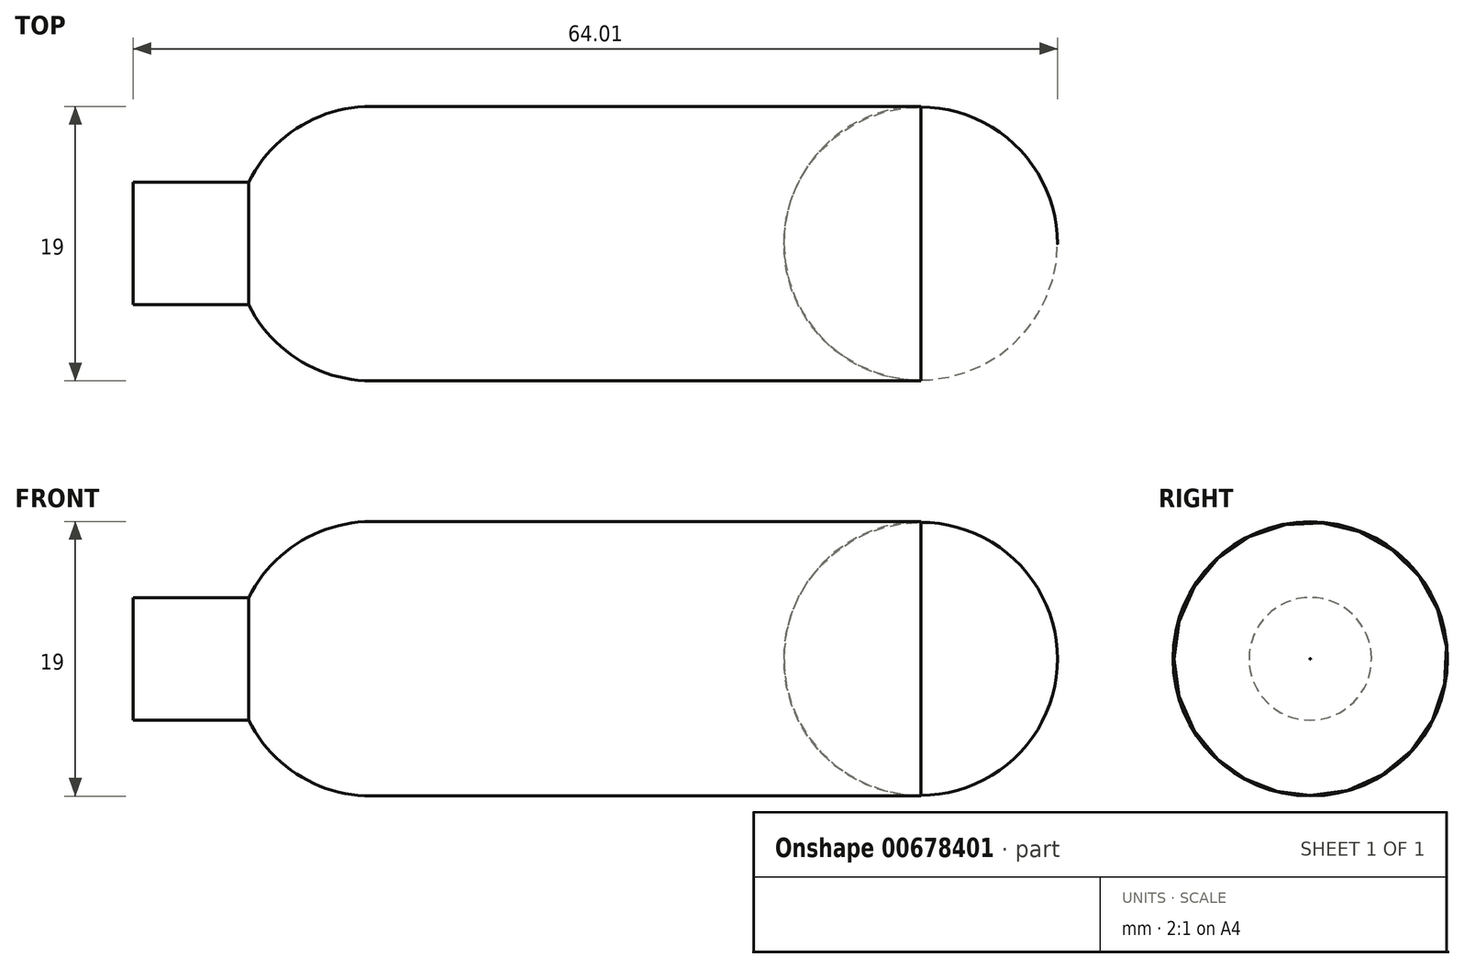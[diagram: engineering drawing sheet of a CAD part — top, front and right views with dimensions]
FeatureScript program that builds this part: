
annotation { "Feature Type Name" : "Feature", "Feature Type Description" : "" }
export const myFeature = defineFeature(function(context is Context, id is Id, definition is map)
    precondition{}
    {
        {
            var Q0;
            Q0=qCreatedBy(makeId("Front.planeOp"),FACE);
            var sketch = newSketch(context, id + "F0", { "sketchPlane" : qUnion([Q0])});
            skLineSegment(sketch, "E0", {"start": v(0, 0) * mm, "end": v(64, 0) * mm});
            skLineSegment(sketch, "E1", {"start": v(0, 0) * mm, "end": v(0, 4.24) * mm});
            skLineSegment(sketch, "E2", {"start": v(0, 4.24) * mm, "end": v(8, 4.24) * mm});
            skLineSegment(sketch, "E3", {"start": v(64, 0) * mm, "end": v(64, 9.5) * mm});
            skLineSegment(sketch, "E4", {"start": v(64, 9.5) * mm, "end": v(8, 9.5) * mm});
            skLineSegment(sketch, "E5", {"start": v(8, 9.5) * mm, "end": v(8, 4.24) * mm});
            skPoint(sketch, "E6", {"position": v(36, 9.5) * mm});
            skLineSegment(sketch, "E7", {"start": v(36, 9.5) * mm, "end": v(56, 9.5) * mm});
            skLineSegment(sketch, "E8", {"start": v(36, 9.5) * mm, "end": v(16, 9.5) * mm});
            skSolve(sketch);
        }
        {
            var Q0;
            Q0=makeQuery(id+"F0.imprint","IMPRINT",FACE,{"disambiguationData":[TD([[makeQuery(id+"F0.imprint","IMPRINT",EDGE,{"derivedFrom":sQuery(id+"F0.wireOp",EDGE,"E0")}),1.0]])]});
            var Q1;
            Q1=sQuery(id+"F0.wireOp",EDGE,"E0");
            revolve(context, id + "F1", {"entities" : qUnion([Q0]), "axis" : qUnion([Q1]), "revolveType" : RevolveType.FULL});
        }
        {
            var Q0;
            Q0=makeQuery(id+"F1.opRevolve","SWEPT_FACE",FACE,{"disambiguationData":[OSD([sQuery(id+"F0.wireOp",EDGE,"E4"),sQuery(id+"F0.wireOp",EDGE,"E7"),sQuery(id+"F0.wireOp",EDGE,"E8")])]});
            fillet(context, id + "F2", {"entities" : qUnion([Q0]), "radius" : 9.47 * mm, "tangentPropagation" : true, "allowEdgeOverflow" : false});
        }
    });
